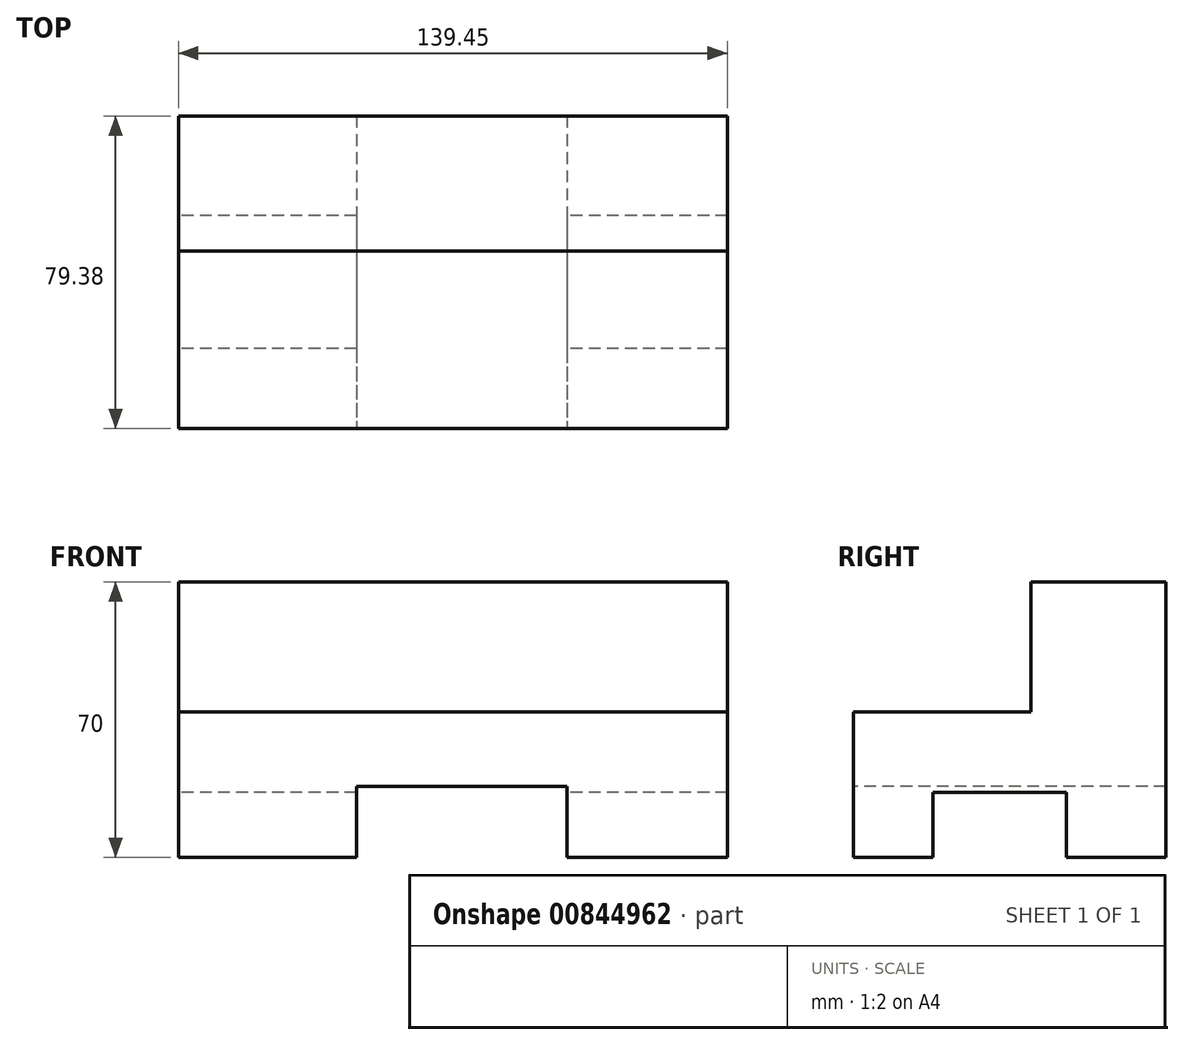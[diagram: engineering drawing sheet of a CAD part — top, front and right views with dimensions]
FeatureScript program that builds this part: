
annotation { "Feature Type Name" : "Feature", "Feature Type Description" : "" }
export const myFeature = defineFeature(function(context is Context, id is Id, definition is map)
    precondition{}
    {
        {
            var Q0;
            Q0=qCreatedBy(makeId("Top.planeOp"),FACE);
            var sketch = newSketch(context, id + "F0", { "sketchPlane" : qUnion([Q0])});
            skLineSegment(sketch, "E0.bottom", {"start": v(-71.45, 50.14) * mm, "end": v(68, 50.14) * mm});
            skLineSegment(sketch, "E0.top", {"start": v(-71.45, -54.24) * mm, "end": v(68, -54.24) * mm});
            skLineSegment(sketch, "E0.left", {"start": v(-71.45, 50.14) * mm, "end": v(-71.45, -54.24) * mm});
            skLineSegment(sketch, "E0.right", {"start": v(68, 50.14) * mm, "end": v(68, -54.24) * mm});
            skSolve(sketch);
        }
        {
            var Q0;
            Q0=makeQuery(id+"F0.imprint","IMPRINT",FACE,{"disambiguationData":[TD([[makeQuery(id+"F0.imprint","IMPRINT",EDGE,{"derivedFrom":sQuery(id+"F0.wireOp",EDGE,"E0.bottom")}),-1.0]])]});
            extrude(context, id + "F1", {"entities" : qUnion([Q0]), "depth" : 10 * mm, "offsetDistance" : 25.4 * mm});
        }
        {
            var Q0;
            Q0=makeQuery(id+"F1.opExtrude","CAP_FACE",FACE,{"disambiguationData":[OSD([sQuery(id+"F0.wireOp",EDGE,"E0.bottom"),sQuery(id+"F0.wireOp",EDGE,"E0.top"),sQuery(id+"F0.wireOp",EDGE,"E0.left"),sQuery(id+"F0.wireOp",EDGE,"E0.right")])],"isStart":false});
            var sketch = newSketch(context, id + "F2", { "sketchPlane" : qUnion([Q0])});
            skLineSegment(sketch, "E1.bottom", {"start": v(-71.45, 50.14) * mm, "end": v(68, 50.14) * mm});
            skLineSegment(sketch, "E1.top", {"start": v(-71.45, 15.84) * mm, "end": v(68, 15.84) * mm});
            skLineSegment(sketch, "E1.left", {"start": v(-71.45, 50.14) * mm, "end": v(-71.45, 15.84) * mm});
            skLineSegment(sketch, "E1.right", {"start": v(68, 50.14) * mm, "end": v(68, 15.84) * mm});
            skSolve(sketch);
        }
        {
            var Q0;
            Q0=makeQuery(id+"F2.imprint","IMPRINT",FACE,{"disambiguationData":[TD([[makeQuery(id+"F2.imprint","IMPRINT",EDGE,{"derivedFrom":sQuery(id+"F2.wireOp",EDGE,"E1.bottom")}),-1.0]])]});
            extrude(context, id + "F3", {"entities" : qUnion([Q0]), "operationType" : NewBodyOperationType.ADD, "depth" : 50 * mm, "offsetDistance" : 25 * mm});
        }
        {
            var Q0;
            Q0=makeQuery(id+"F1.opExtrude","CAP_FACE",FACE,{"disambiguationData":[OSD([sQuery(id+"F0.wireOp",EDGE,"E0.bottom"),sQuery(id+"F0.wireOp",EDGE,"E0.top"),sQuery(id+"F0.wireOp",EDGE,"E0.left"),sQuery(id+"F0.wireOp",EDGE,"E0.right")])],"isStart":false});
            extrude(context, id + "F4", {"entities" : qUnion([Q0]), "operationType" : NewBodyOperationType.ADD, "depth" : 27 * mm, "offsetDistance" : 25 * mm});
        }
        {
            var Q0;
            Q0=makeQuery(id+"F3.opExtrude","CAP_FACE",FACE,{"disambiguationData":[OSD([sQuery(id+"F2.wireOp",EDGE,"E1.bottom"),sQuery(id+"F2.wireOp",EDGE,"E1.top"),sQuery(id+"F2.wireOp",EDGE,"E1.left"),sQuery(id+"F2.wireOp",EDGE,"E1.right")])],"isStart":false});
            extrude(context, id + "F5", {"entities" : qUnion([Q0]), "operationType" : NewBodyOperationType.ADD, "depth" : 10 * mm, "offsetDistance" : 25 * mm});
        }
        {
            var Q0;
            {var subQ0=sQuery(id+"F0.wireOp",EDGE,"E0.top");Q0=makeQuery(id+"F4.boolean.opBoolean","MERGE",FACE,{"derivedFrom":[makeQuery(id+"F1.opExtrude","SWEPT_FACE",FACE,{"disambiguationData":[OSD([subQ0])]}),makeQuery(id+"F4.opExtrude","SWEPT_FACE",FACE,{"disambiguationData":[OSD([subQ0])]})]});}
            extrude(context, id + "F6", {"entities" : qUnion([Q0]), "operationType" : NewBodyOperationType.REMOVE, "oppositeDirection" : true, "depth" : 25 * mm, "offsetDistance" : 25 * mm});
        }
        {
            var Q0;
            Q0=makeQuery(id+"F6.boolean.opBoolean","COPY",FACE,{"derivedFrom":makeQuery(id+"F6.opExtrude","CAP_FACE",FACE,{"disambiguationData":[OSD([sQuery(id+"F0.wireOp",EDGE,"E0.top")])],"isStart":false})});
            var sketch = newSketch(context, id + "F7", { "sketchPlane" : qUnion([Q0])});
            skLineSegment(sketch, "E2.bottom", {"start": v(-26.2, 18.02) * mm, "end": v(27.3, 18.02) * mm});
            skLineSegment(sketch, "E2.top", {"start": v(-26.2, 0) * mm, "end": v(27.3, 0) * mm});
            skLineSegment(sketch, "E2.left", {"start": v(-26.2, 18.02) * mm, "end": v(-26.2, 0) * mm});
            skLineSegment(sketch, "E2.right", {"start": v(27.3, 18.02) * mm, "end": v(27.3, 0) * mm});
            skSolve(sketch);
        }
        {
            var Q0;
            Q0 = qSketchRegion(id + "F7", true);
            extrude(context, id + "F8", {"entities" : qUnion([Q0]), "operationType" : NewBodyOperationType.REMOVE, "oppositeDirection" : true, "depth" : 81 * mm, "offsetDistance" : 25 * mm});
        }
        {
            var Q0;
            {var subQ0=sQuery(id+"F2.wireOp",EDGE,"E1.left");var subQ1=sQuery(id+"F0.wireOp",EDGE,"E0.left");Q0=makeQuery(id+"F5.boolean.opBoolean","MERGE",FACE,{"derivedFrom":[makeQuery(id+"F4.boolean.opBoolean","MERGE",FACE,{"derivedFrom":[makeQuery(id+"F3.boolean.opBoolean","MERGE",FACE,{"derivedFrom":[makeQuery(id+"F1.opExtrude","SWEPT_FACE",FACE,{"disambiguationData":[OSD([subQ1])]}),makeQuery(id+"F3.opExtrude","SWEPT_FACE",FACE,{"disambiguationData":[OSD([subQ0])]})]}),makeQuery(id+"F4.opExtrude","SWEPT_FACE",FACE,{"disambiguationData":[OSD([subQ1])]})]}),makeQuery(id+"F5.opExtrude","SWEPT_FACE",FACE,{"disambiguationData":[OSD([subQ0])]})]});}
            var sketch = newSketch(context, id + "F9", { "sketchPlane" : qUnion([Q0])});
            skLineSegment(sketch, "E3.bottom", {"start": v(-24.9, 16.5) * mm, "end": v(8.96, 16.5) * mm});
            skLineSegment(sketch, "E3.top", {"start": v(-24.9, 0) * mm, "end": v(8.96, 0) * mm});
            skLineSegment(sketch, "E3.left", {"start": v(-24.9, 16.5) * mm, "end": v(-24.9, 0) * mm});
            skLineSegment(sketch, "E3.right", {"start": v(8.96, 16.5) * mm, "end": v(8.96, 0) * mm});
            skSolve(sketch);
        }
        {
            var Q0;
            Q0=makeQuery(id+"F9.imprint","IMPRINT",FACE,{"disambiguationData":[TD([[makeQuery(id+"F9.imprint","IMPRINT",EDGE,{"derivedFrom":sQuery(id+"F9.wireOp",EDGE,"E3.bottom")}),-1.0]])]});
            extrude(context, id + "F10", {"entities" : qUnion([Q0]), "operationType" : NewBodyOperationType.REMOVE, "oppositeDirection" : true, "depth" : 258 * mm, "offsetDistance" : 25 * mm});
        }
    });
